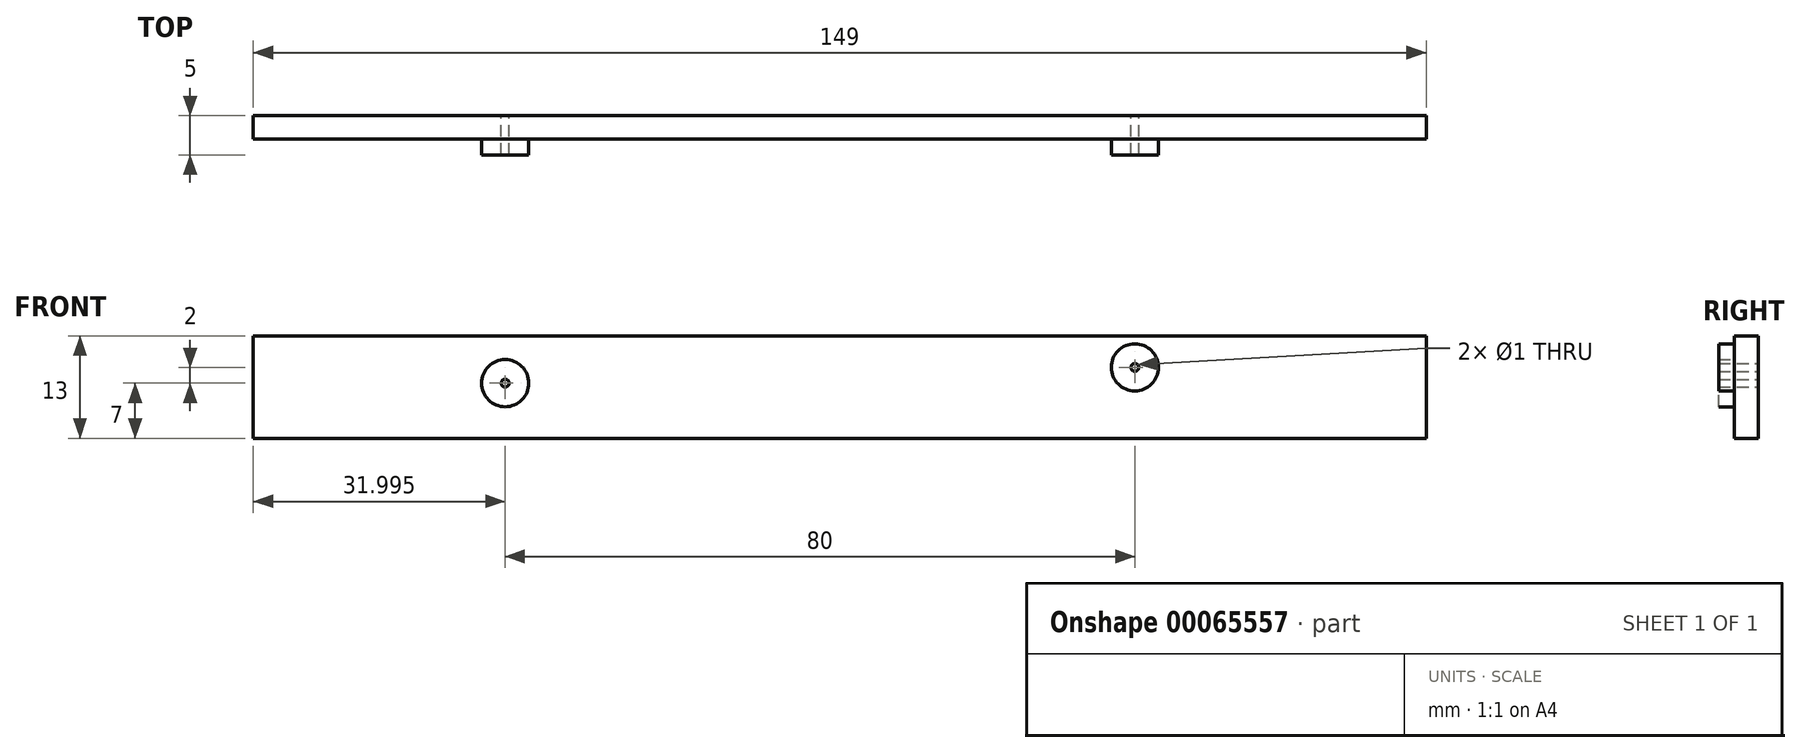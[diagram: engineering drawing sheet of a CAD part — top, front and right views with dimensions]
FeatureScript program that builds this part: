
annotation { "Feature Type Name" : "Feature", "Feature Type Description" : "" }
export const myFeature = defineFeature(function(context is Context, id is Id, definition is map)
    precondition{}
    {
        {
            var Q0;
            Q0=qCreatedBy(makeId("Front.planeOp"),FACE);
            var sketch = newSketch(context, id + "F0", { "sketchPlane" : qUnion([Q0])});
            skLineSegment(sketch, "E0.bottom", {"start": v(-78.74, 0) * mm, "end": v(70.26, 0) * mm});
            skLineSegment(sketch, "E0.top", {"start": v(-78.74, -13) * mm, "end": v(70.26, -13) * mm});
            skLineSegment(sketch, "E0.left", {"start": v(-78.74, 0) * mm, "end": v(-78.74, -13) * mm});
            skLineSegment(sketch, "E0.right", {"start": v(70.26, 0) * mm, "end": v(70.26, -13) * mm});
            skPoint(sketch, "E1", {"position": v(33.26, -4) * mm});
            skPoint(sketch, "E2", {"position": v(-46.74, -6) * mm});
            skSolve(sketch);
        }
        {
            var Q0;
            Q0 = qSketchRegion(id + "F0", true);
            extrude(context, id + "F1", {"entities" : qUnion([Q0]), "depth" : 3 * mm});
        }
        {
            var Q0;
            Q0=makeQuery(id+"F1.opExtrude","CAP_FACE",FACE,{"disambiguationData":[OSD([sQuery(id+"F0.wireOp",EDGE,"E0.bottom"),sQuery(id+"F0.wireOp",EDGE,"E0.top"),sQuery(id+"F0.wireOp",EDGE,"E0.left"),sQuery(id+"F0.wireOp",EDGE,"E0.right")])],"isStart":false});
            var sketch = newSketch(context, id + "F2", { "sketchPlane" : qUnion([Q0])});
            skCircle(sketch, "E3", {"center": v(-46.74, -6) * mm, "radius": 3 * mm});
            skCircle(sketch, "E4", {"center": v(33.26, -4) * mm, "radius": 3 * mm});
            skSolve(sketch);
        }
        {
            var Q0;
            Q0 = qSketchRegion(id + "F2", true);
            extrude(context, id + "F3", {"entities" : qUnion([Q0]), "operationType" : NewBodyOperationType.ADD, "depth" : 2 * mm});
        }
        {
            var Q0;
            Q0=sQuery(id+"F0.wireOp",VERTEX,"E2");
            var Q1;
            Q1=sQuery(id+"F0.wireOp",VERTEX,"E1");
            var Q2;
            Q2=makeQuery(id+"F1.opExtrude","SWEPT_BODY",BODY,{"disambiguationData":[OSD([sQuery(id+"F0.wireOp",EDGE,"E0.bottom"),sQuery(id+"F0.wireOp",EDGE,"E0.top"),sQuery(id+"F0.wireOp",EDGE,"E0.left"),sQuery(id+"F0.wireOp",EDGE,"E0.right")])]});
            hole(context, id + "F4", {"style" : HoleStyle.SIMPLE, "holeDiameter" : 1 * mm, "endStyle" : HoleEndStyle.THROUGH, "oppositeDirection" : true, "locations" : qUnion([Q0, Q1]), "scope" : qUnion([Q2])});
        }
    });
